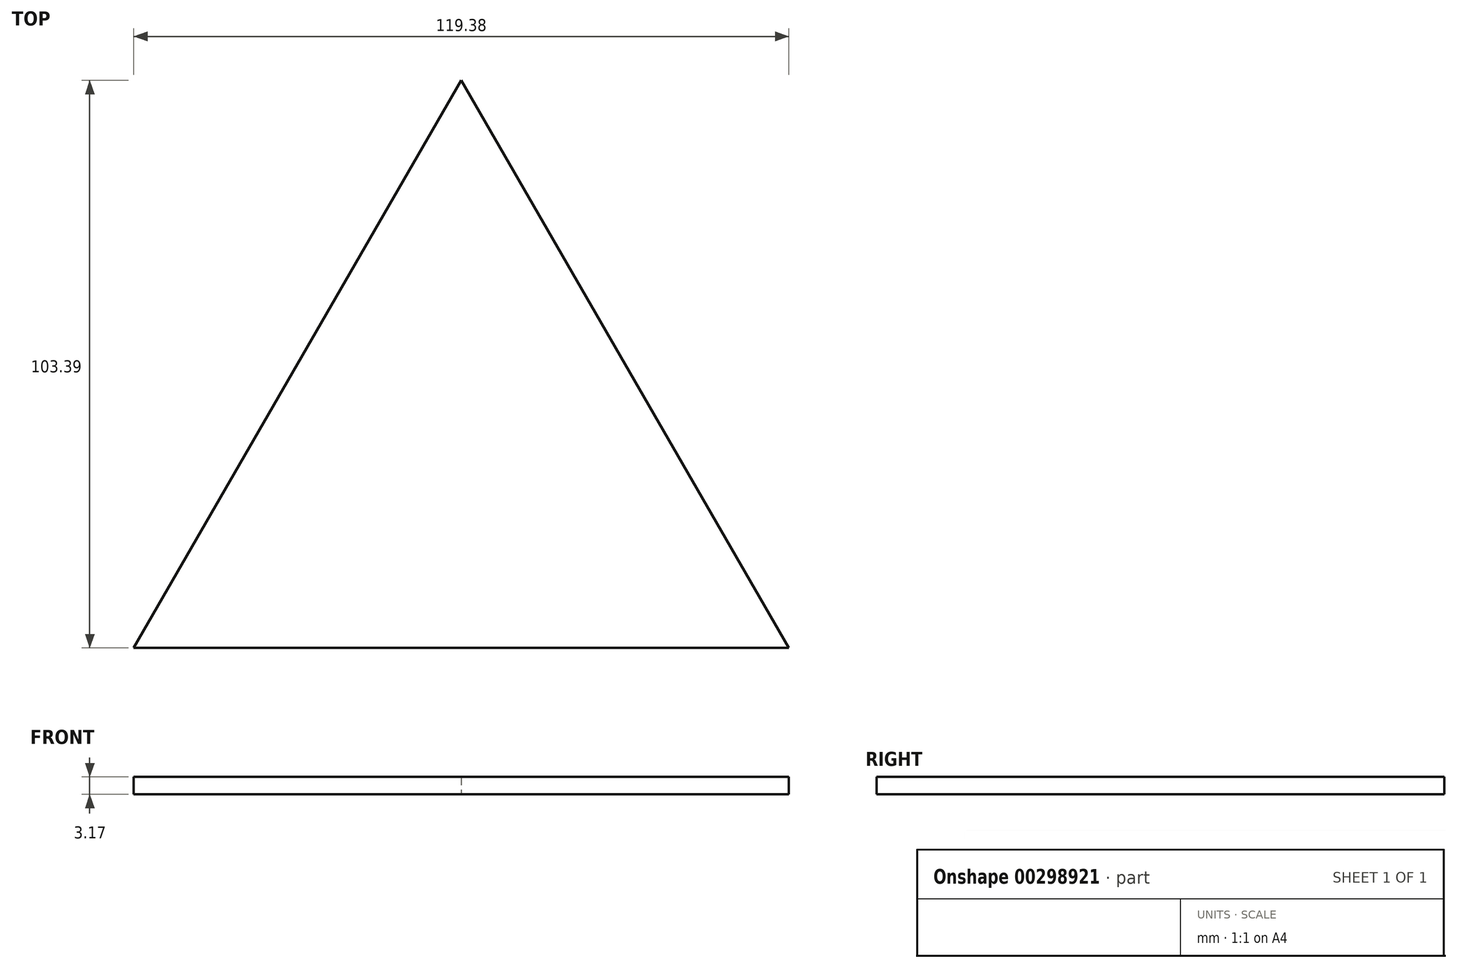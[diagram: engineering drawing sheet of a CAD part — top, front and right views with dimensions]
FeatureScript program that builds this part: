
annotation { "Feature Type Name" : "Feature", "Feature Type Description" : "" }
export const myFeature = defineFeature(function(context is Context, id is Id, definition is map)
    precondition{}
    {
        {
            var Q0;
            Q0=qCreatedBy(makeId("Top.planeOp"),FACE);
            var sketch = newSketch(context, id + "F0", { "sketchPlane" : qUnion([Q0])});
            skLineSegment(sketch, "E0", {"start": v(-59.7, -34.47) * mm, "end": v(-0.01, 68.92) * mm});
            skLineSegment(sketch, "E1", {"start": v(-59.7, -34.47) * mm, "end": v(59.68, -34.47) * mm});
            skLineSegment(sketch, "E2", {"start": v(-0.01, 68.92) * mm, "end": v(59.68, -34.47) * mm});
            skSolve(sketch);
        }
        {
            var Q0;
            Q0=makeQuery(id+"F0.imprint","IMPRINT",FACE,{"disambiguationData":[TD([[makeQuery(id+"F0.imprint","IMPRINT",EDGE,{"derivedFrom":sQuery(id+"F0.wireOp",EDGE,"E0")}),-1.0]])]});
            extrude(context, id + "F1", {"entities" : qUnion([Q0]), "depth" : 3.17 * mm, "offsetDistance" : 25.4 * mm});
        }
    });
